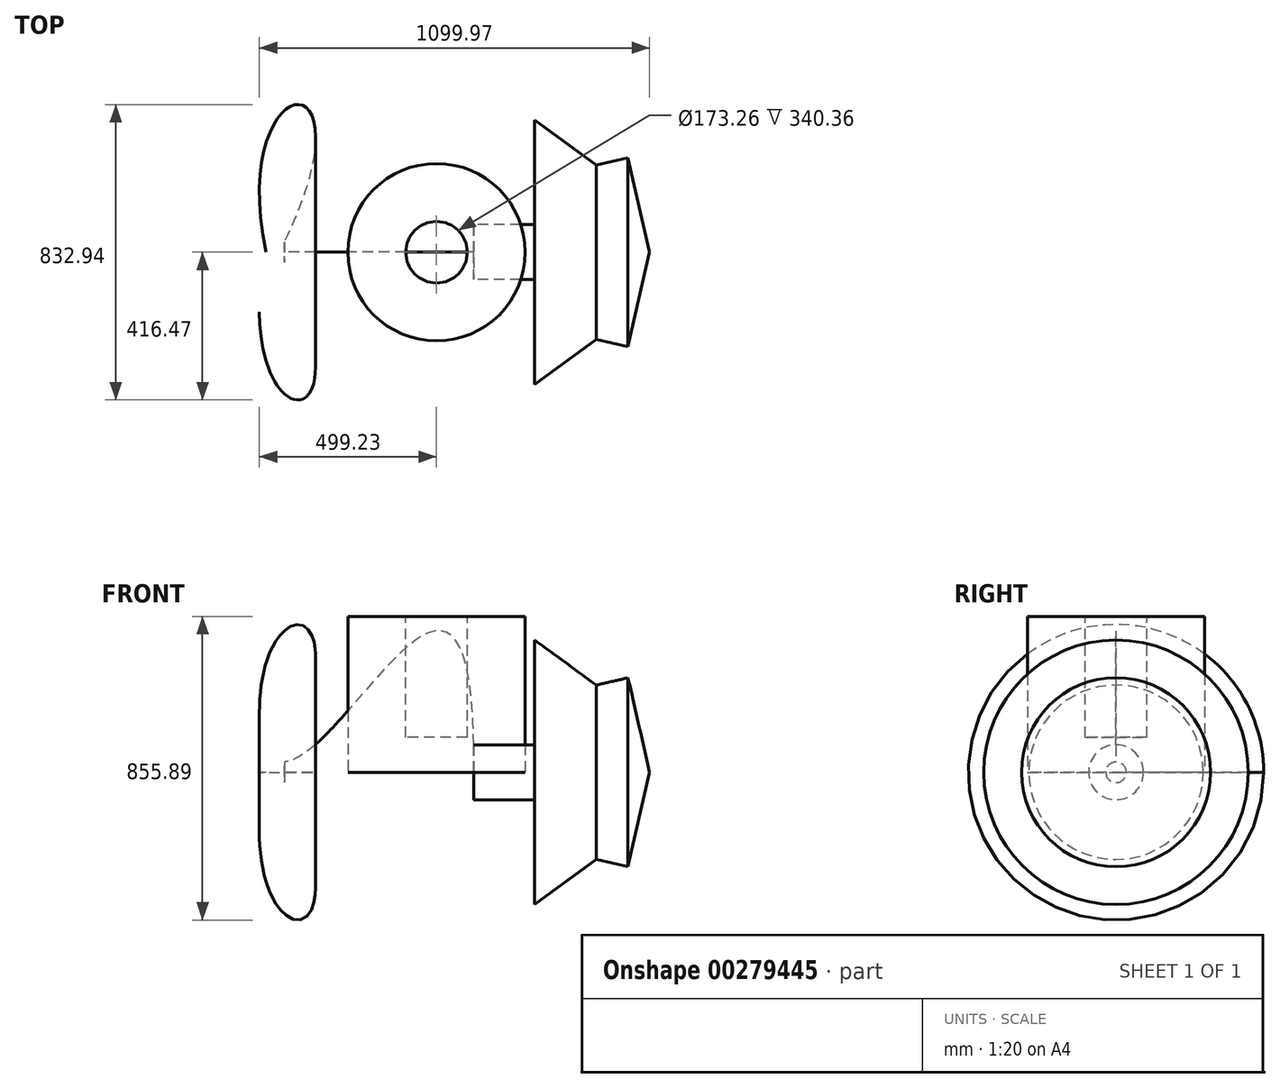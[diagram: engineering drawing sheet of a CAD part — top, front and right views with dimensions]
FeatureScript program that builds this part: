
annotation { "Feature Type Name" : "Feature", "Feature Type Description" : "" }
export const myFeature = defineFeature(function(context is Context, id is Id, definition is map)
    precondition{}
    {
        {
            var Q0;
            Q0=qCreatedBy(makeId("Top.planeOp"),FACE);
            var sketch = newSketch(context, id + "F0", { "sketchPlane" : qUnion([Q0])});
            skCircle(sketch, "E0", {"center": v(0, 0) * mm, "radius": 249.97 * mm});
            skSolve(sketch);
        }
        {
            var Q0;
            Q0 = qSketchRegion(id + "F0", true);
            extrude(context, id + "F1", {"entities" : qUnion([Q0]), "depth" : 439.42 * mm});
        }
        {
            var Q0;
            Q0=makeQuery(id+"F1.opExtrude","CAP_FACE",FACE,{"disambiguationData":[OSD([sQuery(id+"F0.wireOp",EDGE,"E0")])],"isStart":false});
            var sketch = newSketch(context, id + "F2", { "sketchPlane" : qUnion([Q0])});
            skCircle(sketch, "E1", {"center": v(0, 0) * mm, "radius": 86.63 * mm});
            skSolve(sketch);
        }
        {
            var Q0;
            Q0 = qSketchRegion(id + "F2", true);
            extrude(context, id + "F3", {"entities" : qUnion([Q0]), "operationType" : NewBodyOperationType.REMOVE, "oppositeDirection" : true, "depth" : 340.36 * mm});
        }
        {
            var Q0;
            Q0=qCreatedBy(makeId("Top.planeOp"),FACE);
            var sketch = newSketch(context, id + "F4", { "sketchPlane" : qUnion([Q0])});
            skLineSegment(sketch, "E2", {"start": v(-480.02, 0) * mm, "end": v(600.74, 0) * mm});
            skLineSegment(sketch, "E3", {"start": v(600.74, 0) * mm, "end": v(539.67, 266.29) * mm});
            skLineSegment(sketch, "E4", {"start": v(539.67, 266.29) * mm, "end": v(450.03, 245.73) * mm});
            skLineSegment(sketch, "E5", {"start": v(450.03, 245.73) * mm, "end": v(276.94, 372.8) * mm});
            skLineSegment(sketch, "E6", {"start": v(276.94, 372.8) * mm, "end": v(276.94, 77.4) * mm});
            skLineSegment(sketch, "E7", {"start": v(276.94, 77.4) * mm, "end": v(105.1, 77.4) * mm});
            skFitSpline(sketch, "E8", {"points": [v(105.1, 77.4) * mm, v(-428.9, 29.11) * mm], "startDerivative": vector(-38.35, 2232.53) * mm, "endDerivative": vector(-534, -48.29) * mm});
            skFitSpline(sketch, "E9", {"points": [v(-480.02, 0) * mm, v(-428.9, 29.11) * mm], "startDerivative": vector(-336.58, 1565.76) * mm, "endDerivative": vector(-792.46, -1644.58) * mm});
            skSolve(sketch);
        }
        {
            var Q0;
            Q0=makeQuery(id+"F4.imprint","IMPRINT",FACE,{"disambiguationData":[TD([[makeQuery(id+"F4.imprint","IMPRINT",EDGE,{"derivedFrom":sQuery(id+"F4.wireOp",EDGE,"E2")}),1.0]])]});
            var Q1;
            Q1=sQuery(id+"F4.wireOp",EDGE,"E2");
            revolve(context, id + "F5", {"entities" : qUnion([Q0]), "axis" : qUnion([Q1]), "revolveType" : RevolveType.FULL});
        }
    });
